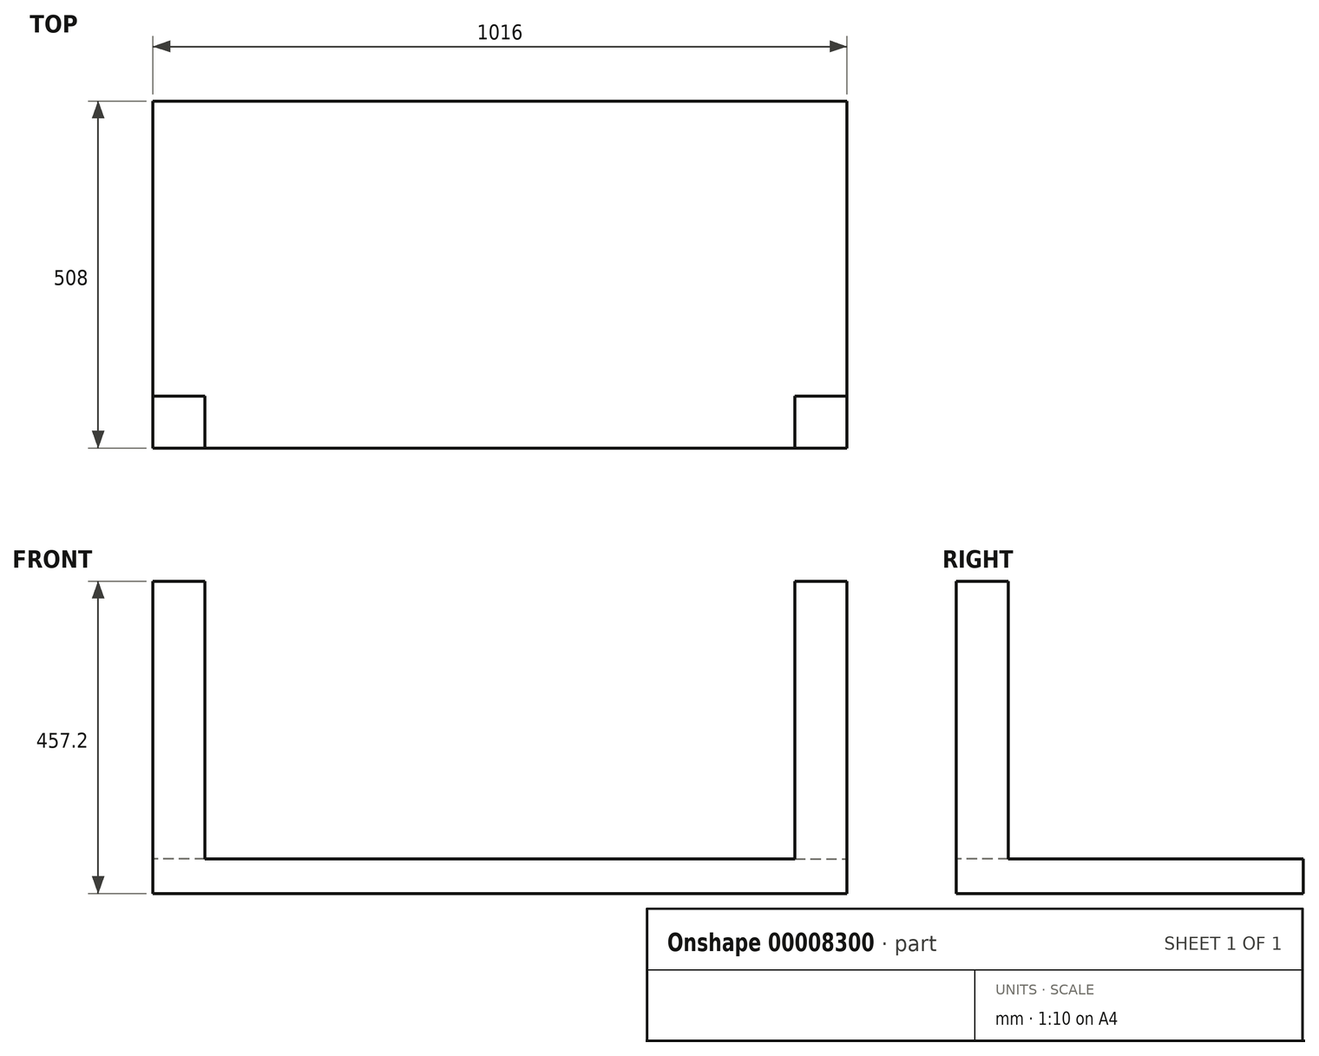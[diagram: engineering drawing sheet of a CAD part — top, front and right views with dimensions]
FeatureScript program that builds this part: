
annotation { "Feature Type Name" : "Feature", "Feature Type Description" : "" }
export const myFeature = defineFeature(function(context is Context, id is Id, definition is map)
    precondition{}
    {
        {
            var Q0;
            Q0=qCreatedBy(makeId("Top.planeOp"),FACE);
            var sketch = newSketch(context, id + "F0", { "sketchPlane" : qUnion([Q0])});
            skLineSegment(sketch, "E0.bottom", {"start": v(-483.12, 517.26) * mm, "end": v(532.88, 517.26) * mm});
            skLineSegment(sketch, "E0.top", {"start": v(-483.12, 9.26) * mm, "end": v(532.88, 9.26) * mm});
            skLineSegment(sketch, "E0.left", {"start": v(-483.12, 517.26) * mm, "end": v(-483.12, 9.26) * mm});
            skLineSegment(sketch, "E0.right", {"start": v(532.88, 517.26) * mm, "end": v(532.88, 9.26) * mm});
            skLineSegment(sketch, "E1.bottom", {"start": v(-483.12, 517.26) * mm, "end": v(-406.92, 517.26) * mm});
            skLineSegment(sketch, "E1.top", {"start": v(-483.12, 441.06) * mm, "end": v(-406.92, 441.06) * mm});
            skLineSegment(sketch, "E1.left", {"start": v(-483.12, 517.26) * mm, "end": v(-483.12, 441.06) * mm});
            skLineSegment(sketch, "E1.right", {"start": v(-406.92, 517.26) * mm, "end": v(-406.92, 441.06) * mm});
            skLineSegment(sketch, "E2.bottom", {"start": v(456.68, 517.26) * mm, "end": v(532.88, 517.26) * mm});
            skLineSegment(sketch, "E2.top", {"start": v(456.68, 441.06) * mm, "end": v(532.88, 441.06) * mm});
            skLineSegment(sketch, "E2.left", {"start": v(456.68, 517.26) * mm, "end": v(456.68, 441.06) * mm});
            skLineSegment(sketch, "E2.right", {"start": v(532.88, 517.26) * mm, "end": v(532.88, 441.06) * mm});
            skLineSegment(sketch, "E3.bottom", {"start": v(-406.92, 85.46) * mm, "end": v(-483.12, 85.46) * mm});
            skLineSegment(sketch, "E3.top", {"start": v(-406.92, 9.26) * mm, "end": v(-483.12, 9.26) * mm});
            skLineSegment(sketch, "E3.left", {"start": v(-406.92, 85.46) * mm, "end": v(-406.92, 9.26) * mm});
            skLineSegment(sketch, "E3.right", {"start": v(-483.12, 85.46) * mm, "end": v(-483.12, 9.26) * mm});
            skLineSegment(sketch, "E4.bottom", {"start": v(456.68, 85.46) * mm, "end": v(532.88, 85.46) * mm});
            skLineSegment(sketch, "E4.top", {"start": v(456.68, 9.26) * mm, "end": v(532.88, 9.26) * mm});
            skLineSegment(sketch, "E4.left", {"start": v(456.68, 85.46) * mm, "end": v(456.68, 9.26) * mm});
            skLineSegment(sketch, "E4.right", {"start": v(532.88, 85.46) * mm, "end": v(532.88, 9.26) * mm});
            skSolve(sketch);
        }
        {
            var Q0;
            Q0=makeQuery(id+"F0.imprint","IMPRINT",FACE,{"disambiguationData":[TD([[makeQuery(id+"F0.imprint","IMPRINT",EDGE,{"derivedFrom":sQuery(id+"F0.wireOp",EDGE,"E3.bottom")}),1.0]])]});
            var Q1;
            Q1=makeQuery(id+"F0.imprint","IMPRINT",FACE,{"disambiguationData":[TD([[makeQuery(id+"F0.imprint","IMPRINT",EDGE,{"derivedFrom":sQuery(id+"F0.wireOp",EDGE,"E1.bottom")}),-1.0]])]});
            var Q2;
            Q2=makeQuery(id+"F0.imprint","IMPRINT",FACE,{"disambiguationData":[TD([[makeQuery(id+"F0.imprint","IMPRINT",EDGE,{"derivedFrom":sQuery(id+"F0.wireOp",EDGE,"E2.bottom")}),-1.0]])]});
            var Q3;
            Q3=makeQuery(id+"F0.imprint","IMPRINT",FACE,{"disambiguationData":[TD([[makeQuery(id+"F0.imprint","IMPRINT",EDGE,{"derivedFrom":sQuery(id+"F0.wireOp",EDGE,"E4.bottom")}),-1.0]])]});
            extrude(context, id + "F1", {"entities" : qUnion([Q0, Q1, Q2, Q3]), "depth" : 457.2 * mm});
        }
        {
            var Q0;
            Q0=qCreatedBy(makeId("Top.planeOp"),FACE);
            var sketch = newSketch(context, id + "F2", { "sketchPlane" : qUnion([Q0])});
            skPoint(sketch, "E5", {"position": v(-483.12, 517.26) * mm});
            skPoint(sketch, "E6", {"position": v(532.88, 517.26) * mm});
            skPoint(sketch, "E7", {"position": v(532.88, 9.26) * mm});
            skPoint(sketch, "E8", {"position": v(-483.12, 9.26) * mm});
            skLineSegment(sketch, "E9.bottom", {"start": v(-483.12, 517.26) * mm, "end": v(532.88, 517.26) * mm});
            skLineSegment(sketch, "E9.top", {"start": v(-483.12, 9.26) * mm, "end": v(532.88, 9.26) * mm});
            skLineSegment(sketch, "E9.left", {"start": v(-483.12, 517.26) * mm, "end": v(-483.12, 9.26) * mm});
            skLineSegment(sketch, "E9.right", {"start": v(532.88, 517.26) * mm, "end": v(532.88, 9.26) * mm});
            skSolve(sketch);
        }
        {
            var Q0;
            Q0 = qSketchRegion(id + "F2", true);
            extrude(context, id + "F3", {"entities" : qUnion([Q0]), "operationType" : NewBodyOperationType.ADD, "depth" : 50.8 * mm});
        }
    });
